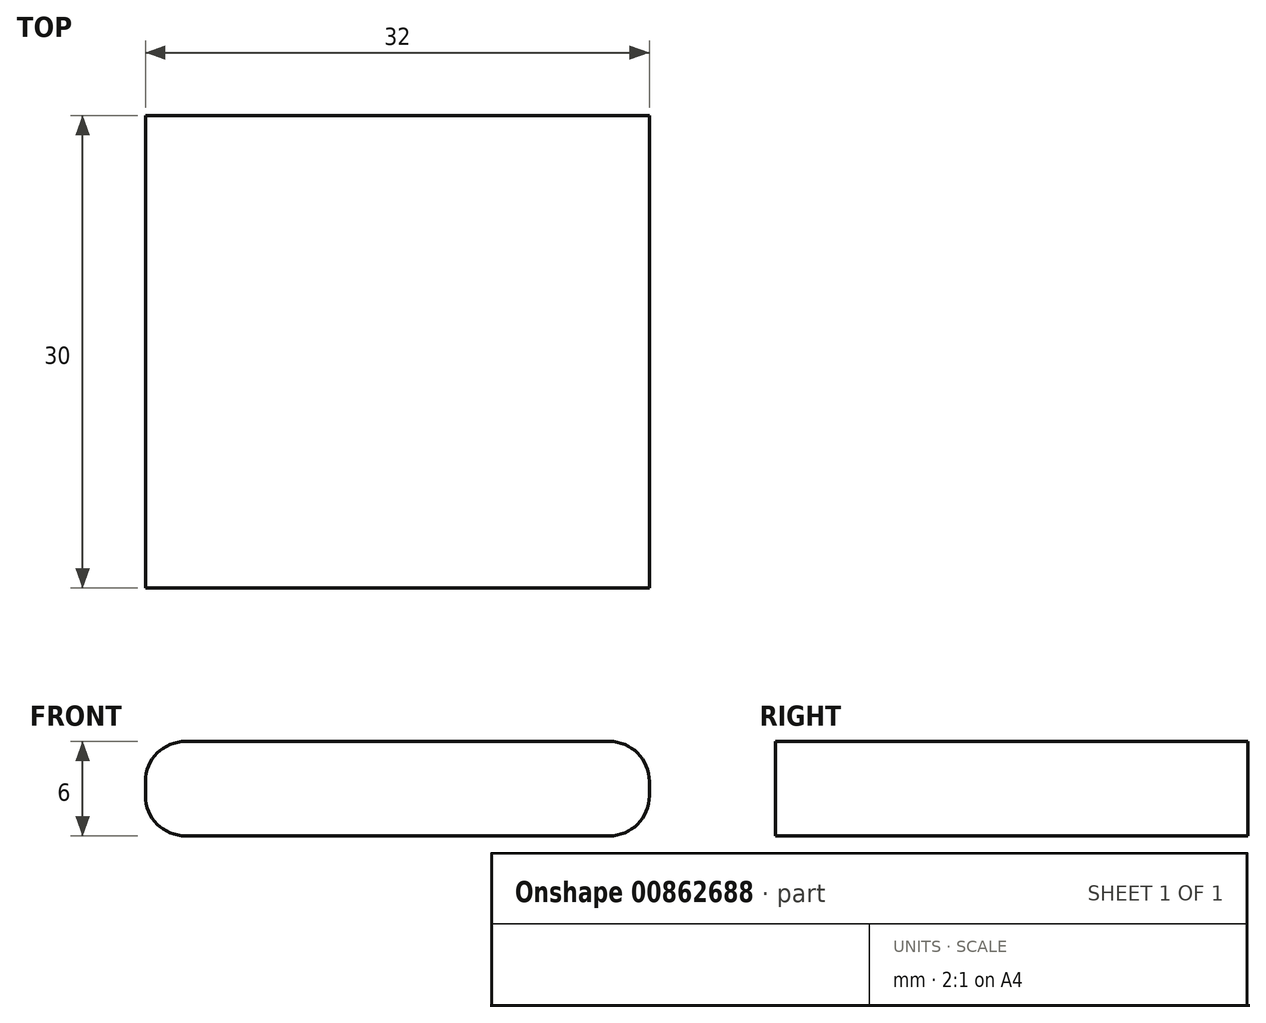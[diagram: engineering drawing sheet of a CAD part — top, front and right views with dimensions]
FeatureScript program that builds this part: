
annotation { "Feature Type Name" : "Feature", "Feature Type Description" : "" }
export const myFeature = defineFeature(function(context is Context, id is Id, definition is map)
    precondition{}
    {
        {
            var Q0;
            Q0=qCreatedBy(makeId("Top.planeOp"),FACE);
            var sketch = newSketch(context, id + "F0", { "sketchPlane" : qUnion([Q0])});
            skLineSegment(sketch, "E0.bottom", {"start": v(16, 15) * mm, "end": v(-16, 15) * mm});
            skLineSegment(sketch, "E0.top", {"start": v(16, -15) * mm, "end": v(-16, -15) * mm});
            skLineSegment(sketch, "E0.left", {"start": v(16, 15) * mm, "end": v(16, -15) * mm});
            skLineSegment(sketch, "E0.right", {"start": v(-16, 15) * mm, "end": v(-16, -15) * mm});
            skPoint(sketch, "E0.middle", {"position": v(0, 0) * mm});
            skSolve(sketch);
        }
        {
            var Q0;
            Q0=makeQuery(id+"F0.imprint","IMPRINT",FACE,{"disambiguationData":[TD([[makeQuery(id+"F0.imprint","IMPRINT",EDGE,{"derivedFrom":sQuery(id+"F0.wireOp",EDGE,"E0.bottom")}),1.0]])]});
            extrude(context, id + "F1", {"entities" : qUnion([Q0]), "depth" : 6 * mm, "offsetDistance" : 25.4 * mm});
        }
        {
            var Q0;
            Q0=makeQuery(id+"F1.opExtrude","CAP_EDGE",EDGE,{"disambiguationData":[OSD([sQuery(id+"F0.wireOp",EDGE,"E0.right")])],"isStart":false});
            var Q1;
            Q1=makeQuery(id+"F1.opExtrude","CAP_EDGE",EDGE,{"disambiguationData":[OSD([sQuery(id+"F0.wireOp",EDGE,"E0.right")])],"isStart":true});
            var Q2;
            Q2=makeQuery(id+"F1.opExtrude","CAP_EDGE",EDGE,{"disambiguationData":[OSD([sQuery(id+"F0.wireOp",EDGE,"E0.left")])],"isStart":false});
            var Q3;
            Q3=makeQuery(id+"F1.opExtrude","CAP_EDGE",EDGE,{"disambiguationData":[OSD([sQuery(id+"F0.wireOp",EDGE,"E0.left")])],"isStart":true});
            fillet(context, id + "F2", {"entities" : qUnion([Q0, Q1, Q2, Q3]), "radius" : 2.54 * mm, "tangentPropagation" : true, "allowEdgeOverflow" : false});
        }
    });
